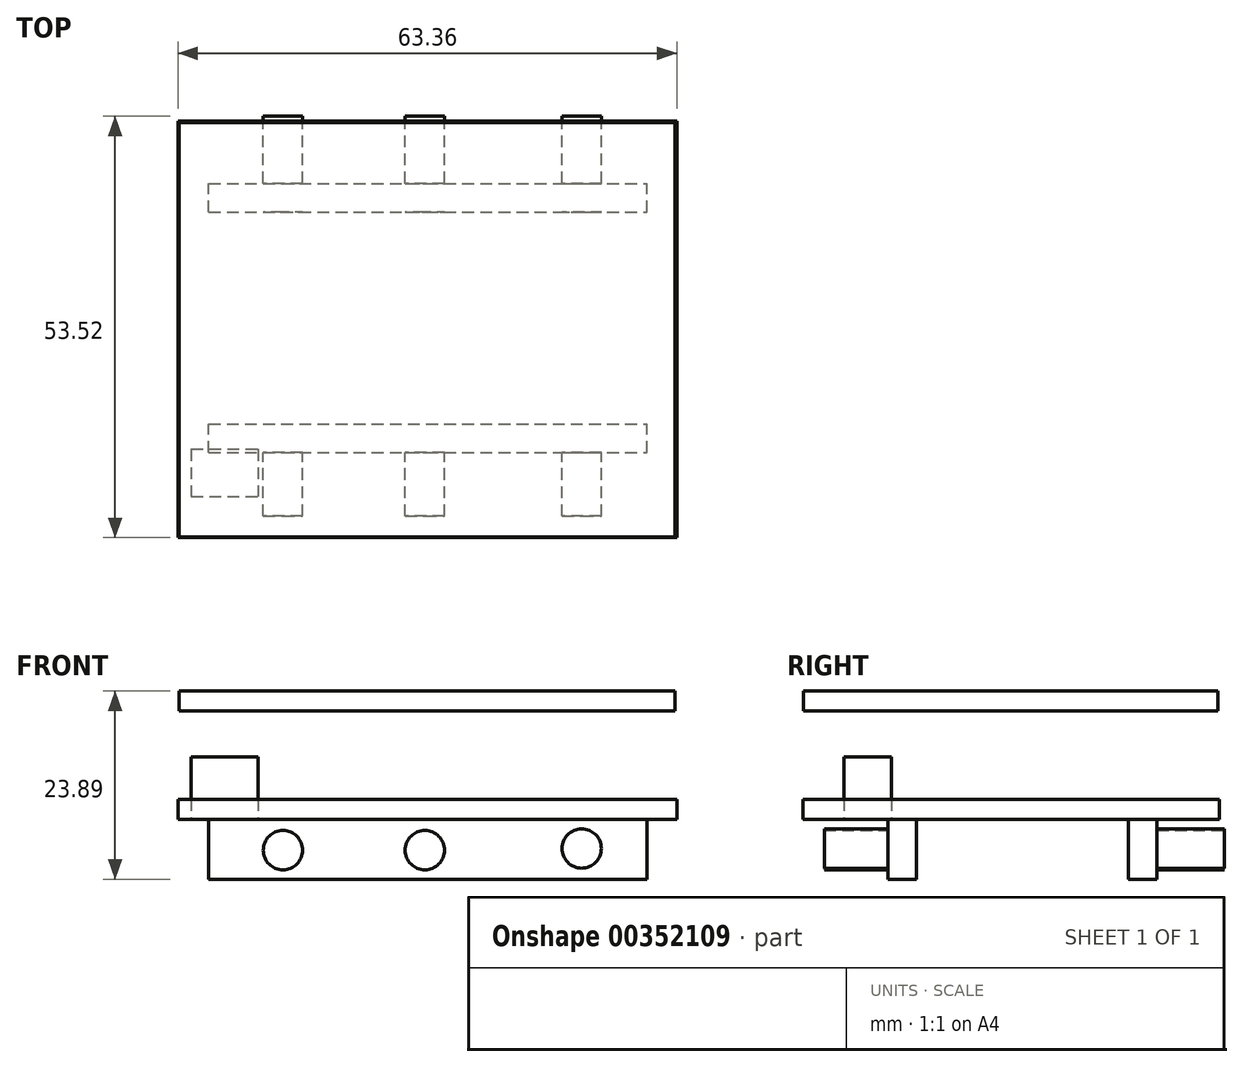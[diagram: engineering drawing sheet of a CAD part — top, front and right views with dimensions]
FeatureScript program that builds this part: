
annotation { "Feature Type Name" : "Feature", "Feature Type Description" : "" }
export const myFeature = defineFeature(function(context is Context, id is Id, definition is map)
    precondition{}
    {
        {
            var Q0;
            Q0=qCreatedBy(makeId("Top.planeOp"),FACE);
            var sketch = newSketch(context, id + "F0", { "sketchPlane" : qUnion([Q0])});
            skLineSegment(sketch, "E0.bottom", {"start": v(-30.08, 24.8) * mm, "end": v(33.28, 24.8) * mm});
            skLineSegment(sketch, "E0.top", {"start": v(-30.08, -28.12) * mm, "end": v(33.28, -28.12) * mm});
            skLineSegment(sketch, "E0.left", {"start": v(-30.08, 24.8) * mm, "end": v(-30.08, -28.12) * mm});
            skLineSegment(sketch, "E0.right", {"start": v(33.28, 24.8) * mm, "end": v(33.28, -28.12) * mm});
            skSolve(sketch);
        }
        {
            var Q0;
            Q0 = qSketchRegion(id + "F0", true);
            extrude(context, id + "F1", {"entities" : qUnion([Q0]), "depth" : 2.54 * mm});
        }
        {
            var Q0;
            Q0=qCreatedBy(makeId("Right.planeOp"),FACE);
            var sketch = newSketch(context, id + "F2", { "sketchPlane" : qUnion([Q0])});
            skLineSegment(sketch, "E1.bottom", {"start": v(24.61, 16.27) * mm, "end": v(-28.06, 16.27) * mm});
            skLineSegment(sketch, "E1.top", {"start": v(24.61, 13.73) * mm, "end": v(-28.06, 13.73) * mm});
            skLineSegment(sketch, "E1.left", {"start": v(24.61, 16.27) * mm, "end": v(24.61, 13.73) * mm});
            skLineSegment(sketch, "E1.right", {"start": v(-28.06, 16.27) * mm, "end": v(-28.06, 13.73) * mm});
            skSolve(sketch);
        }
        {
            var Q0;
            Q0 = qSketchRegion(id + "F2", true);
            extrude(context, id + "F3", {"entities" : qUnion([Q0]), "oppositeDirection" : true, "depth" : 29.97 * mm, "hasSecondDirection" : true, "secondDirectionOppositeDirection" : false, "secondDirectionDepth" : 33.02 * mm});
        }
        {
            var Q0;
            Q0=qCreatedBy(makeId("Top.planeOp"),FACE);
            var sketch = newSketch(context, id + "F4", { "sketchPlane" : qUnion([Q0])});
            skLineSegment(sketch, "E2.bottom", {"start": v(-26.18, -17.33) * mm, "end": v(29.5, -17.33) * mm});
            skLineSegment(sketch, "E2.top", {"start": v(-26.18, -13.66) * mm, "end": v(29.5, -13.66) * mm});
            skLineSegment(sketch, "E2.left", {"start": v(-26.18, -17.33) * mm, "end": v(-26.18, -13.66) * mm});
            skLineSegment(sketch, "E2.right", {"start": v(29.5, -17.33) * mm, "end": v(29.5, -13.66) * mm});
            skLineSegment(sketch, "E3.bottom", {"start": v(-26.18, 13.2) * mm, "end": v(29.5, 13.2) * mm});
            skLineSegment(sketch, "E3.top", {"start": v(-26.18, 16.88) * mm, "end": v(29.5, 16.88) * mm});
            skLineSegment(sketch, "E3.left", {"start": v(-26.18, 13.2) * mm, "end": v(-26.18, 16.88) * mm});
            skLineSegment(sketch, "E3.right", {"start": v(29.5, 13.2) * mm, "end": v(29.5, 16.88) * mm});
            skSolve(sketch);
        }
        {
            var Q0;
            Q0 = qSketchRegion(id + "F4", true);
            extrude(context, id + "F5", {"entities" : qUnion([Q0]), "operationType" : NewBodyOperationType.ADD, "oppositeDirection" : true, "depth" : 7.62 * mm});
        }
        {
            var Q0;
            Q0=qCreatedBy(makeId("Front.planeOp"),FACE);
            var sketch = newSketch(context, id + "F6", { "sketchPlane" : qUnion([Q0])});
            skCircle(sketch, "E4", {"center": v(21.2, -3.72) * mm, "radius": 2.5 * mm});
            skCircle(sketch, "E5", {"center": v(-16.76, -3.93) * mm, "radius": 2.5 * mm});
            skCircle(sketch, "E6", {"center": v(1.27, -3.93) * mm, "radius": 2.5 * mm});
            skSolve(sketch);
        }
        {
            var Q0;
            Q0 = qSketchRegion(id + "F6", true);
            extrude(context, id + "F7", {"entities" : qUnion([Q0]), "operationType" : NewBodyOperationType.ADD, "depth" : 25.4 * mm, "hasSecondDirection" : true, "secondDirectionOppositeDirection" : true, "secondDirectionDepth" : 25.4 * mm});
        }
        {
            var Q0;
            Q0=qCreatedBy(makeId("Right.planeOp"),FACE);
            var sketch = newSketch(context, id + "F8", { "sketchPlane" : qUnion([Q0])});
            skLineSegment(sketch, "E7.bottom", {"start": v(13.2, -1.22) * mm, "end": v(-13.66, -1.22) * mm});
            skLineSegment(sketch, "E7.top", {"start": v(13.2, -6.45) * mm, "end": v(-13.66, -6.45) * mm});
            skLineSegment(sketch, "E7.left", {"start": v(13.2, -1.22) * mm, "end": v(13.2, -6.45) * mm});
            skLineSegment(sketch, "E7.right", {"start": v(-13.66, -1.22) * mm, "end": v(-13.66, -6.45) * mm});
            skSolve(sketch);
        }
        {
            var Q0;
            Q0 = qSketchRegion(id + "F8", true);
            extrude(context, id + "F9", {"entities" : qUnion([Q0]), "operationType" : NewBodyOperationType.REMOVE, "oppositeDirection" : true, "depth" : 25.4 * mm, "hasSecondDirection" : true, "secondDirectionOppositeDirection" : false, "secondDirectionDepth" : 25.4 * mm});
        }
        {
            var Q0;
            Q0=qCreatedBy(makeId("Top.planeOp"),FACE);
            var sketch = newSketch(context, id + "F10", { "sketchPlane" : qUnion([Q0])});
            skLineSegment(sketch, "E8.bottom", {"start": v(-28.4, -16.88) * mm, "end": v(-19.9, -16.88) * mm});
            skLineSegment(sketch, "E8.top", {"start": v(-28.4, -22.9) * mm, "end": v(-19.9, -22.9) * mm});
            skLineSegment(sketch, "E8.left", {"start": v(-28.4, -16.88) * mm, "end": v(-28.4, -22.9) * mm});
            skLineSegment(sketch, "E8.right", {"start": v(-19.9, -16.88) * mm, "end": v(-19.9, -22.9) * mm});
            skSolve(sketch);
        }
        {
            var Q0;
            Q0 = qSketchRegion(id + "F10", true);
            extrude(context, id + "F11", {"entities" : qUnion([Q0]), "depth" : 7.92 * mm});
        }
        {
            var Q0;
            Q0=qCreatedBy(makeId("Front.planeOp"),FACE);
            var sketch = newSketch(context, id + "F12", { "sketchPlane" : qUnion([Q0])});
            skLineSegment(sketch, "E9.bottom", {"start": v(-30.15, 16.17) * mm, "end": v(-28.4, 16.17) * mm});
            skLineSegment(sketch, "E9.top", {"start": v(-30.15, 0) * mm, "end": v(-28.4, 0) * mm});
            skLineSegment(sketch, "E9.left", {"start": v(-30.15, 16.17) * mm, "end": v(-30.15, 0) * mm});
            skLineSegment(sketch, "E9.right", {"start": v(-28.4, 16.17) * mm, "end": v(-28.4, 0) * mm});
            skLineSegment(sketch, "E10.bottom", {"start": v(31.54, 16.17) * mm, "end": v(33.29, 16.17) * mm});
            skLineSegment(sketch, "E10.top", {"start": v(31.54, 0) * mm, "end": v(33.29, 0) * mm});
            skLineSegment(sketch, "E10.left", {"start": v(31.54, 16.17) * mm, "end": v(31.54, 0) * mm});
            skLineSegment(sketch, "E10.right", {"start": v(33.29, 16.17) * mm, "end": v(33.29, 0) * mm});
            skSolve(sketch);
        }
        {
            var Q0;
            Q0=sQuery(id+"F12.wireOp",EDGE,"E9.right");
            var Q1;
            Q1=sQuery(id+"F12.wireOp",EDGE,"E10.left");
            var Q2;
            Q2=sQuery(id+"F12.wireOp",EDGE,"E10.right");
            var Q3;
            Q3=sQuery(id+"F12.wireOp",EDGE,"E9.left");
            var Q4;
            Q4=sQuery(id+"F12.wireOp",EDGE,"E10.top");
            var Q5;
            Q5=sQuery(id+"F12.wireOp",EDGE,"E10.bottom");
            var Q6;
            Q6=sQuery(id+"F12.wireOp",EDGE,"E9.bottom");
            var Q7;
            Q7=sQuery(id+"F12.wireOp",EDGE,"E9.top");
            extrude(context, id + "F13", {"bodyType" : ToolBodyType.SURFACE, "surfaceEntities" : qUnion([Q0, Q1, Q2, Q3, Q4, Q5, Q6, Q7]), "depth" : 27.94 * mm, "hasSecondDirection" : true, "secondDirectionOppositeDirection" : true, "secondDirectionDepth" : 24.64 * mm});
        }
    });
